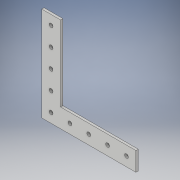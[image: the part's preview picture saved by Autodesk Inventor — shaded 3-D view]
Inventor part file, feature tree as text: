
AUTODESK INVENTOR PART (.ipt)
format: ipt  version: 2018 (Build 220112000, 112)  size: 139,776 bytes
history: native  units: in
note: dims shown in document units (in); Inventor stores cm internally (conversion verified against a paired STEP export)
features: extrude x2, sketch x2
ambient origin geometry x8: Origin, YZ Plane, XZ Plane, XY Plane, X Axis, Y Axis, Z Axis, Center Point
bodies: Solid1 (feature_tree)
feature tree (4):
  extrude  "Extrusion1"  Depth=1.0in
  extrude  "Extrusion2"  Depth=3.0in
  sketch  "Sketch1"  dims[d0=3.0in d1=1.0in]
  sketch  "Sketch2"  dims[d2=1.0in d3=3.0in d4=0.5in d5=1.0in d6=1.0in d7=1.0in d8=1.0in d9=0.2031in d10=0.125in d11=0.0in d12=1.0in d13=1.0in d14=1.0in d15=1.0in d16=2.0in d17=1.0in d18=2.0in d19=0.125in d20=0.0in]
